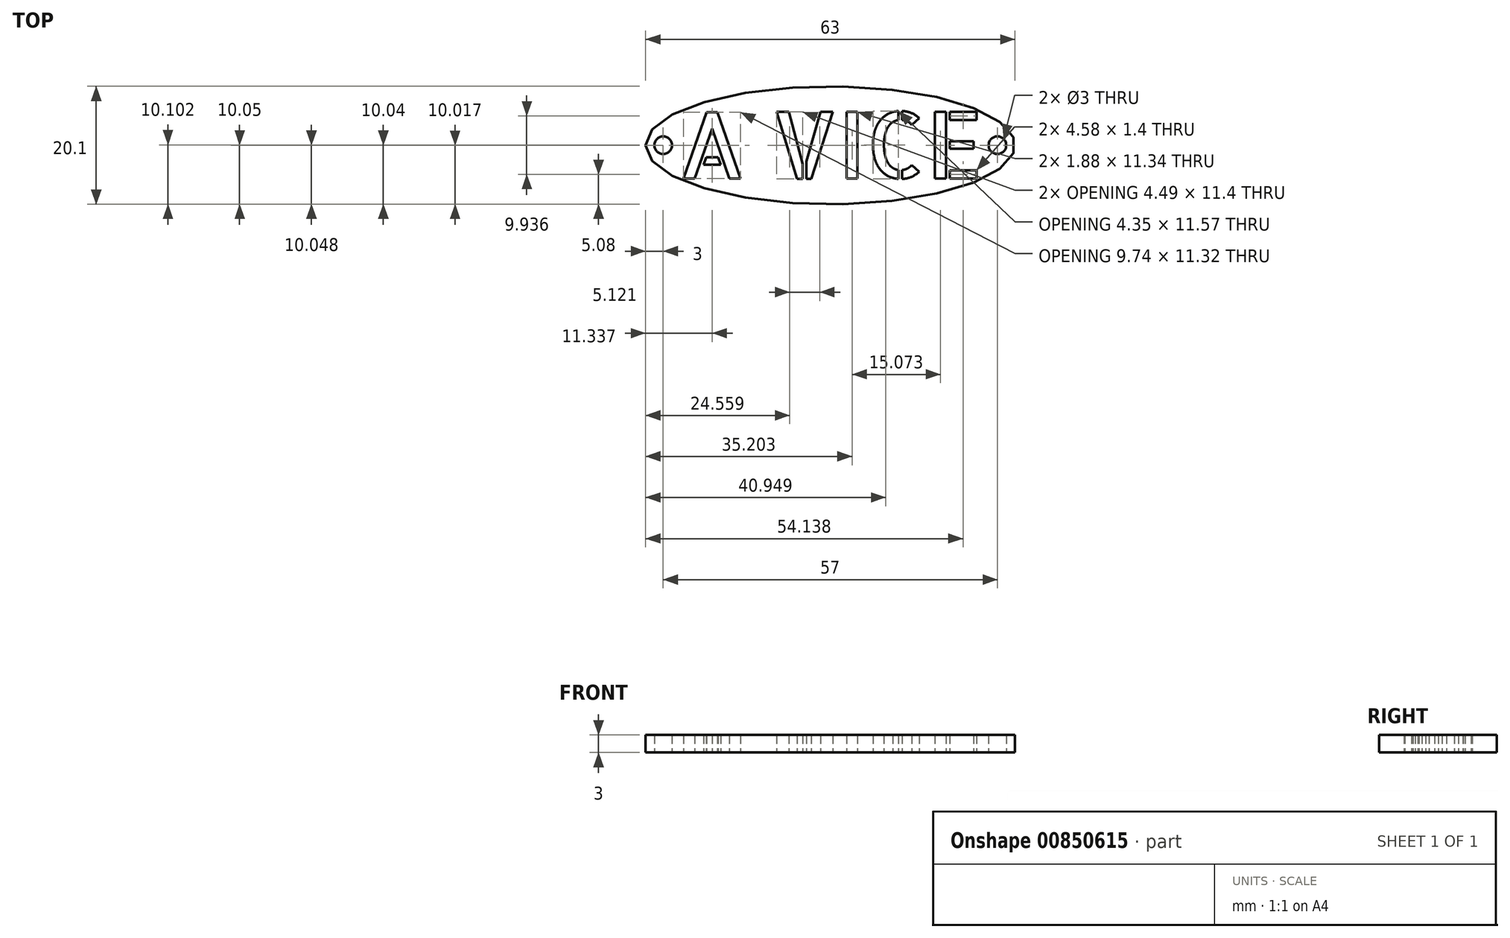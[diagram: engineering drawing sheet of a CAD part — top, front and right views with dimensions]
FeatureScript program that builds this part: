
annotation { "Feature Type Name" : "Feature", "Feature Type Description" : "" }
export const myFeature = defineFeature(function(context is Context, id is Id, definition is map)
    precondition{}
    {
        {
            var Q0;
            Q0=qCreatedBy(makeId("Top.planeOp"),FACE);
            var sketch = newSketch(context, id + "F0", { "sketchPlane" : qUnion([Q0])});
            skEllipse(sketch, "E0", {"center": v(0, 0) * mm, "majorRadius": 31.5 * mm, "minorRadius": 10.05 * mm, "majorAxis": v(-1, 0)});
            skCircle(sketch, "E1", {"center": v(-28.5, 0) * mm, "radius": 1.5 * mm});
            skCircle(sketch, "E2", {"center": v(28.5, 0) * mm, "radius": 1.5 * mm});
            skText(sketch, "E3", { "text": "A VICE", "fontName": "AllertaStencil-Regular.ttf"});
            skLineSegment(sketch, "E4", {"start": v(26, 0) * mm, "end": v(-26, 0) * mm, "construction": true});
            const initialGuessF0  = {"E3": [-0.026, -0.00567, 1, 0, 0.01134]};
            skSetInitialGuess(sketch, initialGuessF0);
            skSolve(sketch);
        }
        {
            var Q0;
            Q0=makeQuery(id+"F0.imprint","IMPRINT",FACE,{"disambiguationData":[TD([[makeQuery(id+"F0.imprint","IMPRINT",EDGE,{"derivedFrom":sQuery(id+"F0.wireOp",EDGE,"E0")}),1.0]])]});
            extrude(context, id + "F1", {"entities" : qUnion([Q0]), "depth" : 3 * mm, "offsetDistance" : 25 * mm});
        }
    });
